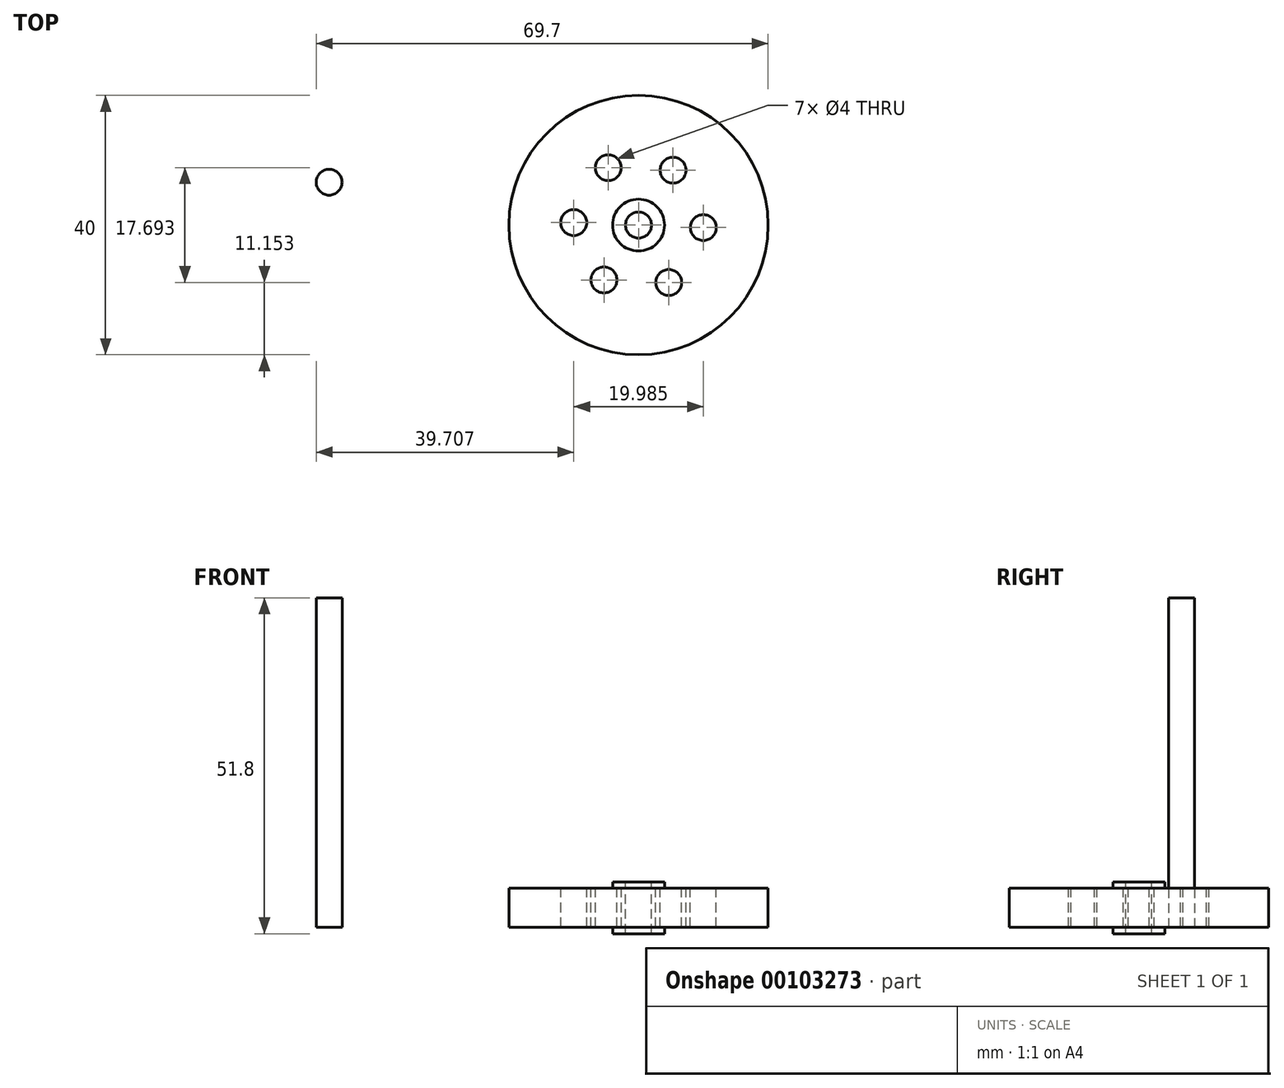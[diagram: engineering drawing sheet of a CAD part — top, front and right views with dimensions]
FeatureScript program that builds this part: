
annotation { "Feature Type Name" : "Feature", "Feature Type Description" : "" }
export const myFeature = defineFeature(function(context is Context, id is Id, definition is map)
    precondition{}
    {
        {
            var Q0;
            Q0=qCreatedBy(makeId("Top.planeOp"),FACE);
            var sketch = newSketch(context, id + "F0", { "sketchPlane" : qUnion([Q0])});
            skCircle(sketch, "E0", {"center": v(0, 0) * mm, "radius": 20 * mm});
            skSolve(sketch);
        }
        {
            var Q0;
            Q0=makeQuery(id+"F0.imprint","IMPRINT",FACE,{"disambiguationData":[TD([[makeQuery(id+"F0.imprint","IMPRINT",EDGE,{"derivedFrom":sQuery(id+"F0.wireOp",EDGE,"E0")}),1.0]])]});
            extrude(context, id + "F1", {"entities" : qUnion([Q0]), "depth" : 6 * mm});
        }
        {
            var Q0;
            Q0=makeQuery(id+"F1.opExtrude","CAP_FACE",FACE,{"disambiguationData":[OSD([sQuery(id+"F0.wireOp",EDGE,"E0")])],"isStart":false});
            var sketch = newSketch(context, id + "F2", { "sketchPlane" : qUnion([Q0])});
            skCircle(sketch, "E1", {"center": v(0, 0) * mm, "radius": 4 * mm});
            skCircle(sketch, "E2", {"center": v(0, 0) * mm, "radius": 2 * mm});
            skCircle(sketch, "E3", {"center": v(5.33, 8.46) * mm, "radius": 2 * mm});
            skCircle(sketch, "E4.1.0", {"center": v(-4.66, 8.85) * mm, "radius": 2 * mm});
            skCircle(sketch, "E4.2.0", {"center": v(-10, 0.39) * mm, "radius": 2 * mm});
            skCircle(sketch, "E4.3.0", {"center": v(-5.33, -8.46) * mm, "radius": 2 * mm});
            skCircle(sketch, "E4.4.0", {"center": v(4.66, -8.85) * mm, "radius": 2 * mm});
            skCircle(sketch, "E4.5.0", {"center": v(10, -0.39) * mm, "radius": 2 * mm});
            skSolve(sketch);
        }
        {
            var Q0;
            Q0=makeQuery(id+"F2.imprint","IMPRINT",FACE,{"disambiguationData":[TD([[makeQuery(id+"F2.imprint","IMPRINT",EDGE,{"derivedFrom":sQuery(id+"F2.wireOp",EDGE,"E4.1.0")}),1.0]])]});
            var Q1;
            Q1=makeQuery(id+"F2.imprint","IMPRINT",FACE,{"disambiguationData":[TD([[makeQuery(id+"F2.imprint","IMPRINT",EDGE,{"derivedFrom":sQuery(id+"F2.wireOp",EDGE,"E3")}),1.0]])]});
            var Q2;
            Q2=makeQuery(id+"F2.imprint","IMPRINT",FACE,{"disambiguationData":[TD([[makeQuery(id+"F2.imprint","IMPRINT",EDGE,{"derivedFrom":sQuery(id+"F2.wireOp",EDGE,"E4.5.0")}),1.0]])]});
            var Q3;
            Q3=makeQuery(id+"F2.imprint","IMPRINT",FACE,{"disambiguationData":[TD([[makeQuery(id+"F2.imprint","IMPRINT",EDGE,{"derivedFrom":sQuery(id+"F2.wireOp",EDGE,"E4.4.0")}),1.0]])]});
            var Q4;
            Q4=makeQuery(id+"F2.imprint","IMPRINT",FACE,{"disambiguationData":[TD([[makeQuery(id+"F2.imprint","IMPRINT",EDGE,{"derivedFrom":sQuery(id+"F2.wireOp",EDGE,"E4.3.0")}),1.0]])]});
            var Q5;
            Q5=makeQuery(id+"F2.imprint","IMPRINT",FACE,{"disambiguationData":[TD([[makeQuery(id+"F2.imprint","IMPRINT",EDGE,{"derivedFrom":sQuery(id+"F2.wireOp",EDGE,"E4.2.0")}),1.0]])]});
            var Q6;
            Q6=makeQuery(id+"F2.imprint","IMPRINT",FACE,{"disambiguationData":[TD([[makeQuery(id+"F2.imprint","IMPRINT",EDGE,{"derivedFrom":sQuery(id+"F2.wireOp",EDGE,"E2")}),1.0]])]});
            extrude(context, id + "F3", {"entities" : qUnion([Q0, Q1, Q2, Q3, Q4, Q5, Q6]), "operationType" : NewBodyOperationType.REMOVE, "endBound" : BoundingType.THROUGH_ALL, "oppositeDirection" : true, "depth" : 25.4 * mm});
        }
        {
            var Q0;
            Q0=makeQuery(id+"F2.imprint","IMPRINT",FACE,{"disambiguationData":[TD([[makeQuery(id+"F2.imprint","IMPRINT",EDGE,{"derivedFrom":sQuery(id+"F2.wireOp",EDGE,"E1")}),1.0]])]});
            extrude(context, id + "F4", {"entities" : qUnion([Q0]), "operationType" : NewBodyOperationType.ADD, "depth" : 1 * mm});
        }
        {
            var Q0;
            Q0=makeQuery(id+"F1.opExtrude","CAP_FACE",FACE,{"disambiguationData":[OSD([sQuery(id+"F0.wireOp",EDGE,"E0")])],"isStart":true});
            var sketch = newSketch(context, id + "F5", { "sketchPlane" : qUnion([Q0])});
            skCircle(sketch, "E5", {"center": v(0, 0) * mm, "radius": 4 * mm});
            skSolve(sketch);
        }
        {
            var Q0;
            Q0=makeQuery(id+"F5.imprint","IMPRINT",FACE,{"disambiguationData":[TD([[makeQuery(id+"F5.imprint","IMPRINT",EDGE,{"derivedFrom":sQuery(id+"F5.wireOp",EDGE,"E5")}),1.0]])]});
            extrude(context, id + "F6", {"entities" : qUnion([Q0]), "operationType" : NewBodyOperationType.ADD, "depth" : 1 * mm});
        }
        {
            var Q0;
            Q0=qCreatedBy(makeId("Top.planeOp"),FACE);
            var sketch = newSketch(context, id + "F7", { "sketchPlane" : qUnion([Q0])});
            skCircle(sketch, "E6", {"center": v(-47.7, 6.6) * mm, "radius": 2 * mm});
            skSolve(sketch);
        }
        {
            var Q0;
            Q0=makeQuery(id+"F7.imprint","IMPRINT",FACE,{"disambiguationData":[TD([[makeQuery(id+"F7.imprint","IMPRINT",EDGE,{"derivedFrom":sQuery(id+"F7.wireOp",EDGE,"E6")}),1.0]])]});
            extrude(context, id + "F8", {"entities" : qUnion([Q0]), "depth" : 50.8 * mm});
        }
    });
